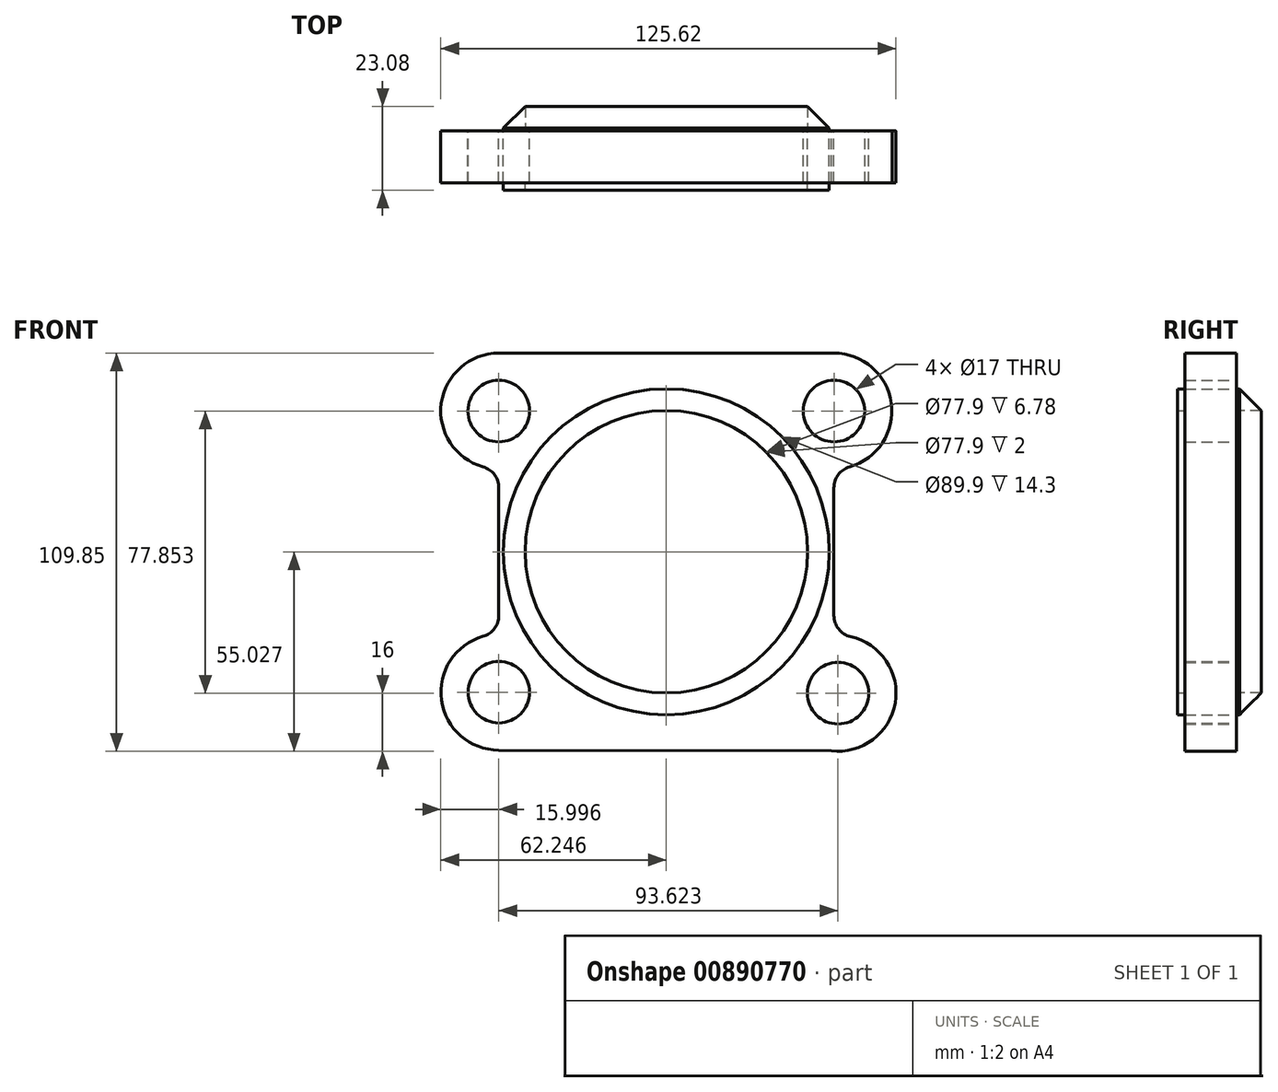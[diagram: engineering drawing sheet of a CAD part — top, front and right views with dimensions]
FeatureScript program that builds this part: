
annotation { "Feature Type Name" : "Feature", "Feature Type Description" : "" }
export const myFeature = defineFeature(function(context is Context, id is Id, definition is map)
    precondition{}
    {
        {
            var Q0;
            Q0=qCreatedBy(makeId("Front.planeOp"),FACE);
            var sketch = newSketch(context, id + "F0", { "sketchPlane" : qUnion([Q0])});
            skArc(sketch, "E0", {"start": v(-123.71, 60.4) * mm, "mid": v(-139.56, 46.6) * mm, "end": v(-128.06, 29) * mm});
            skArc(sketch, "E1", {"start": v(-128.05, -17.76) * mm, "mid": v(-139.53, -35.36) * mm, "end": v(-123.68, -49.16) * mm});
            skArc(sketch, "E2", {"start": v(-31.95, -49.34) * mm, "mid": v(-14.32, -36.14) * mm, "end": v(-26.57, -17.84) * mm});
            skArc(sketch, "E3", {"start": v(-26.87, 29) * mm, "mid": v(-15.37, 46.6) * mm, "end": v(-31.21, 60.4) * mm});
            skLineSegment(sketch, "E4", {"start": v(-123.68, 23.23) * mm, "end": v(-123.68, -12) * mm});
            skLineSegment(sketch, "E5", {"start": v(-31.24, -12) * mm, "end": v(-31.24, 23.23) * mm});
            skLineSegment(sketch, "E6", {"start": v(-123.71, 60.4) * mm, "end": v(-31.21, 60.4) * mm});
            skLineSegment(sketch, "E7", {"start": v(-123.68, -49.16) * mm, "end": v(-31.95, -49.34) * mm});
            skPoint(sketch, "E8.newPointA", {"position": v(-123.71, 28.4) * mm});
            skArc(sketch, "E8.filletArc", {"start": v(-123.68, 23.23) * mm, "mid": v(-124.9, 26.85) * mm, "end": v(-128.06, 29) * mm});
            skPoint(sketch, "E9.newPointA", {"position": v(-123.68, -17.16) * mm});
            skArc(sketch, "E9.filletArc", {"start": v(-128.05, -17.76) * mm, "mid": v(-124.9, -15.6) * mm, "end": v(-123.68, -12) * mm});
            skArc(sketch, "E10.filletArc", {"start": v(-31.24, -12) * mm, "mid": v(-29.93, -15.74) * mm, "end": v(-26.57, -17.84) * mm});
            skArc(sketch, "E11.filletArc", {"start": v(-26.87, 29) * mm, "mid": v(-30.03, 26.85) * mm, "end": v(-31.24, 23.23) * mm});
            skCircle(sketch, "E12", {"center": v(-77.46, 5.58) * mm, "radius": 44.95 * mm});
            skCircle(sketch, "E13", {"center": v(-77.46, 5.58) * mm, "radius": 38.95 * mm});
            skCircle(sketch, "E14", {"center": v(-31.22, 44.4) * mm, "radius": 8.5 * mm});
            skCircle(sketch, "E15", {"center": v(-123.71, 44.4) * mm, "radius": 8.5 * mm});
            skCircle(sketch, "E16", {"center": v(-123.68, -33.16) * mm, "radius": 8.5 * mm});
            skCircle(sketch, "E17", {"center": v(-30.1, -33.45) * mm, "radius": 8.5 * mm});
            skSolve(sketch);
        }
        {
            var Q0;
            Q0=makeQuery(id+"F0.imprint","IMPRINT",FACE,{"disambiguationData":[TD([[makeQuery(id+"F0.imprint","IMPRINT",EDGE,{"derivedFrom":sQuery(id+"F0.wireOp",EDGE,"E0")}),1.0]])]});
            extrude(context, id + "F1", {"entities" : qUnion([Q0]), "depth" : 14.3 * mm, "offsetDistance" : 25.4 * mm});
        }
        {
            var Q0;
            Q0=makeQuery(id+"F0.imprint","IMPRINT",FACE,{"disambiguationData":[TD([[makeQuery(id+"F0.imprint","IMPRINT",EDGE,{"derivedFrom":sQuery(id+"F0.wireOp",EDGE,"E12")}),1.0]])]});
            extrude(context, id + "F2", {"entities" : qUnion([Q0]), "operationType" : NewBodyOperationType.ADD, "oppositeDirection" : true, "depth" : 8.4 * mm, "offsetDistance" : 25.4 * mm});
        }
        {
            var Q0;
            Q0=makeQuery(id+"F1.opExtrude","CAP_FACE",FACE,{"disambiguationData":[OSD([sQuery(id+"F0.wireOp",EDGE,"E0"),sQuery(id+"F0.wireOp",EDGE,"E1"),sQuery(id+"F0.wireOp",EDGE,"E2"),sQuery(id+"F0.wireOp",EDGE,"E3"),sQuery(id+"F0.wireOp",EDGE,"E4"),sQuery(id+"F0.wireOp",EDGE,"E5"),sQuery(id+"F0.wireOp",EDGE,"E6"),sQuery(id+"F0.wireOp",EDGE,"E7"),sQuery(id+"F0.wireOp",EDGE,"E8.filletArc"),sQuery(id+"F0.wireOp",EDGE,"E9.filletArc"),sQuery(id+"F0.wireOp",EDGE,"E10.filletArc"),sQuery(id+"F0.wireOp",EDGE,"E11.filletArc"),sQuery(id+"F0.wireOp",EDGE,"E12")])],"isStart":false});
            var sketch = newSketch(context, id + "F3", { "sketchPlane" : qUnion([Q0])});
            skCircle(sketch, "E18", {"center": v(-77.46, 5.58) * mm, "radius": 38.95 * mm});
            skCircle(sketch, "E19", {"center": v(-77.46, 5.58) * mm, "radius": 44.95 * mm});
            skSolve(sketch);
        }
        {
            var Q0;
            Q0=makeQuery(id+"F3.imprint","IMPRINT",FACE,{"disambiguationData":[TD([[makeQuery(id+"F3.imprint","IMPRINT",EDGE,{"derivedFrom":sQuery(id+"F3.wireOp",EDGE,"E18")}),-1.0]])]});
            extrude(context, id + "F4", {"entities" : qUnion([Q0]), "depth" : 2 * mm, "offsetDistance" : 25.4 * mm});
        }
        {
            var Q0;
            Q0=makeQuery(id+"F2.opExtrude","CAP_EDGE",EDGE,{"disambiguationData":[OSD([sQuery(id+"F0.wireOp",EDGE,"E12")])],"isStart":false});
            chamfer(context, id + "F5", {"entities" : qUnion([Q0]), "width" : 7.62 * mm, "tangentPropagation" : true});
        }
    });
